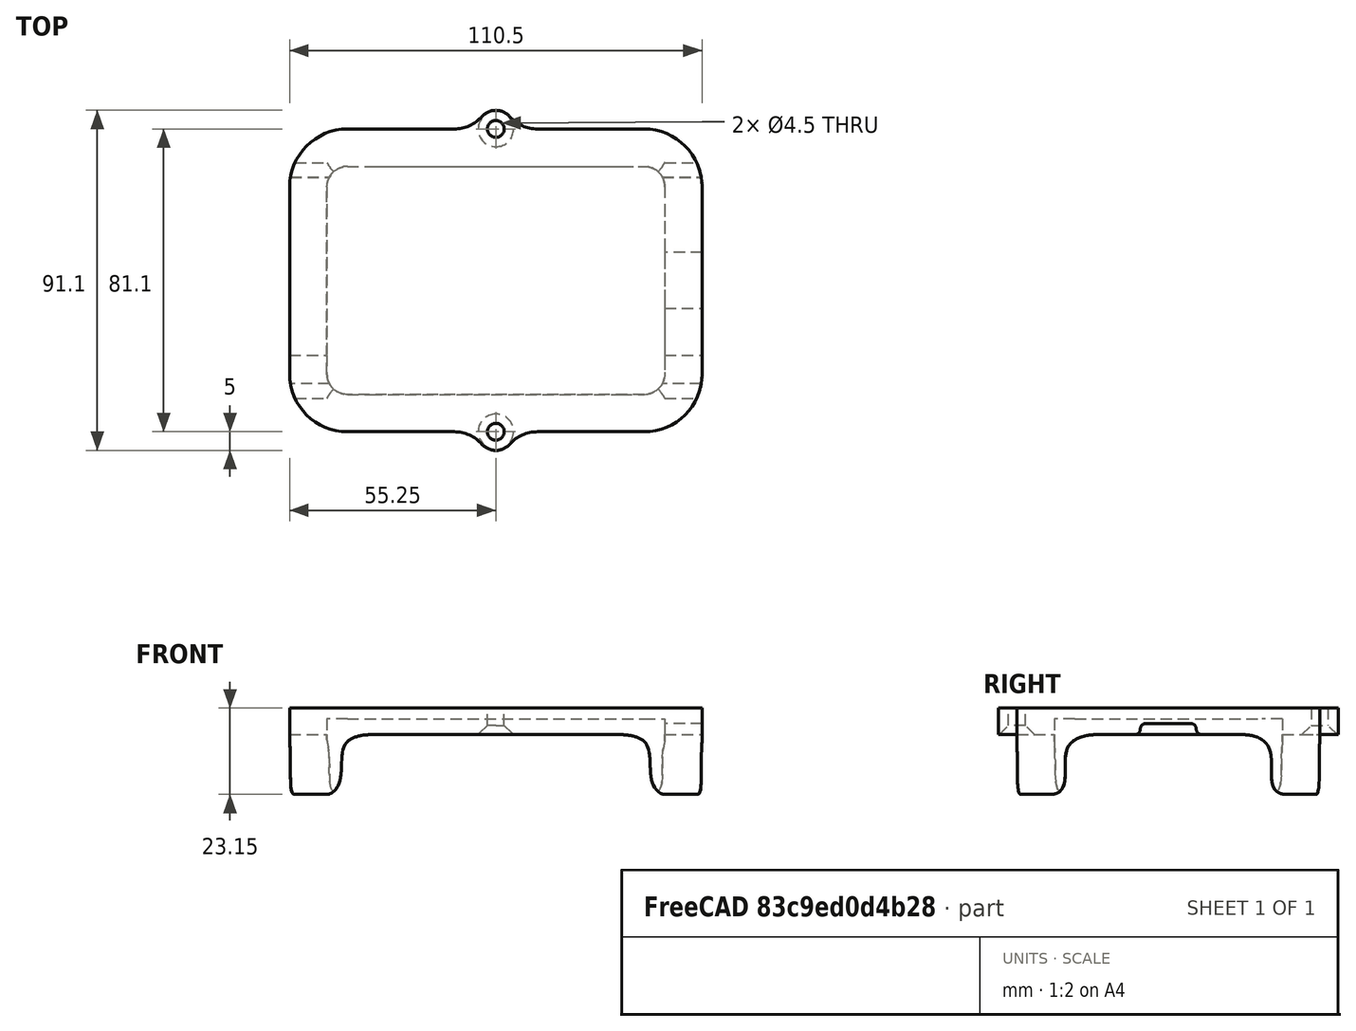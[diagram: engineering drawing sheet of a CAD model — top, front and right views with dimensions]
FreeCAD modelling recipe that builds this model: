
FCSTD DOCUMENT  (FreeCAD 0.22R36340 (Git))
Label: rpi 4 mount
License: All rights reserved
LicenseURL: https://en.wikipedia.org/wiki/All_rights_reserved
objects: Part::Feature×1, PartDesign::FeatureBase×1, Sketcher::SketchObject×1, PartDesign::Pocket×1, PartDesign::Body×1
note: 6 computed .brp shape members not serialized (recipe doc carries the construction recipe); baked Part::Feature solids carry a one-line shape summary decoded from their .brp

FEATURE [Part::Feature] ssd_mount
  shape: bbox 110.5 x 91.1 x 35.4 mm, 74 faces (baked)
FEATURE [PartDesign::FeatureBase] BaseFeature
  BaseFeature = -> ssd_mount
  Suppressed = false
FEATURE [Sketcher::SketchObject] Sketch
  AttachmentSupport = -> [BaseFeature]
  FullyConstrained = false
  MapMode = 5
  Placement = pos=(0,0,20.4) rot=(0,0,1;0rad)
  sketch-geometry (4):
    g0: LineSegment StartX=-63.9409 StartY=51.7566 StartZ=0 EndX=-63.9409 EndY=-51.3293 EndZ=0
    g1: LineSegment StartX=-63.9409 StartY=-51.3293 StartZ=0 EndX=69.2324 EndY=-51.3293 EndZ=0
    g2: LineSegment StartX=69.2324 StartY=-51.3293 StartZ=0 EndX=69.2324 EndY=51.7566 EndZ=0
    g3: LineSegment StartX=69.2324 StartY=51.7566 StartZ=0 EndX=-63.9409 EndY=51.7566 EndZ=0
  constraints (8):
    c: Coincident(g0,g1)
    c: Coincident(g1,g2)
    c: Coincident(g2,g3)
    c: Coincident(g3,g0)
    c: Vertical(g0)
    c: Vertical(g2)
    c: Horizontal(g1)
    c: Horizontal(g3)
FEATURE [PartDesign::Pocket] Pocket
  BaseFeature = -> BaseFeature
  Direction = (0,0,-1)
  Length = 12.25
  Length2 = 5
  Profile = -> Sketch
  ReferenceAxis = -> Sketch [N_Axis]
  Refine = true
  Suppressed = false
  Type = 0
FEATURE [PartDesign::Body] Body
  BaseFeature = -> ssd_mount
  Group = -> [BaseFeature,Sketch,Pocket]
  Origin = -> Origin
  Tip = -> Pocket
